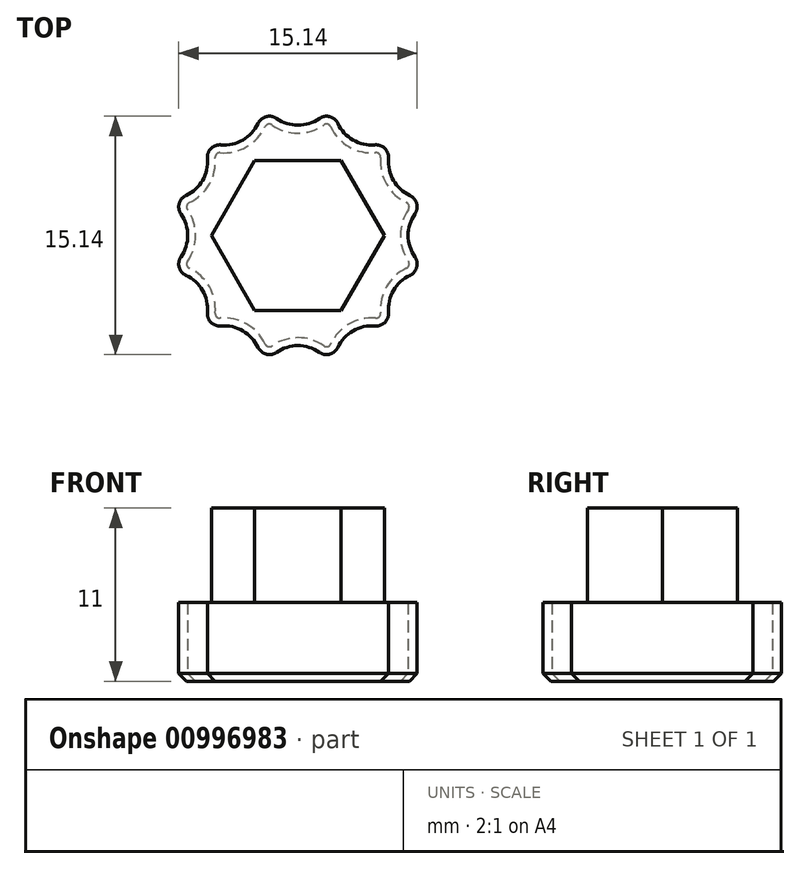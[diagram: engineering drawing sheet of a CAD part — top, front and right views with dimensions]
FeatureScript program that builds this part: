
annotation { "Feature Type Name" : "Feature", "Feature Type Description" : "" }
export const myFeature = defineFeature(function(context is Context, id is Id, definition is map)
    precondition{}
    {
        {
            var Q0;
            Q0=qCreatedBy(makeId("Top.planeOp"),FACE);
            var sketch = newSketch(context, id + "F0", { "sketchPlane" : qUnion([Q0])});
            skCircle(sketch, "E0", {"center": v(0, 0) * mm, "radius": 7 * mm, "construction": true});
            skArc(sketch, "E1", {"start": v(-1.36, 7.43) * mm, "mid": v(0, 7) * mm, "end": v(1.36, 7.43) * mm});
            skArc(sketch, "E2.1.0", {"start": v(-4.9, 5.75) * mm, "mid": v(-3.5, 6.06) * mm, "end": v(-2.53, 7.11) * mm});
            skArc(sketch, "E2.2.0", {"start": v(-7.11, 2.53) * mm, "mid": v(-6.06, 3.5) * mm, "end": v(-5.75, 4.9) * mm});
            skArc(sketch, "E2.3.0", {"start": v(-7.43, -1.36) * mm, "mid": v(-7, 0) * mm, "end": v(-7.43, 1.36) * mm});
            skArc(sketch, "E2.4.0", {"start": v(-5.75, -4.9) * mm, "mid": v(-6.06, -3.5) * mm, "end": v(-7.11, -2.53) * mm});
            skArc(sketch, "E2.5.0", {"start": v(-2.53, -7.11) * mm, "mid": v(-3.5, -6.06) * mm, "end": v(-4.9, -5.75) * mm});
            skArc(sketch, "E2.6.0", {"start": v(1.36, -7.43) * mm, "mid": v(0, -7) * mm, "end": v(-1.36, -7.43) * mm});
            skArc(sketch, "E2.7.0", {"start": v(4.9, -5.75) * mm, "mid": v(3.5, -6.06) * mm, "end": v(2.53, -7.11) * mm});
            skArc(sketch, "E2.8.0", {"start": v(7.11, -2.53) * mm, "mid": v(6.06, -3.5) * mm, "end": v(5.75, -4.9) * mm});
            skArc(sketch, "E2.9.0", {"start": v(7.43, 1.36) * mm, "mid": v(7, 0) * mm, "end": v(7.43, -1.36) * mm});
            skArc(sketch, "E2.10.0", {"start": v(5.75, 4.9) * mm, "mid": v(6.06, 3.5) * mm, "end": v(7.11, 2.53) * mm});
            skArc(sketch, "E2.11.0", {"start": v(2.53, 7.11) * mm, "mid": v(3.5, 6.06) * mm, "end": v(4.9, 5.75) * mm});
            skPoint(sketch, "E3.newPointA", {"position": v(1.9, 7.96) * mm});
            skPoint(sketch, "E3.newPointB", {"position": v(2.33, 7.85) * mm});
            skArc(sketch, "E3.filletArc", {"start": v(2.53, 7.11) * mm, "mid": v(2.02, 7.54) * mm, "end": v(1.36, 7.43) * mm});
            skPoint(sketch, "E4.newPointA", {"position": v(5.63, 5.94) * mm});
            skPoint(sketch, "E4.newPointB", {"position": v(5.94, 5.63) * mm});
            skArc(sketch, "E4.filletArc", {"start": v(5.75, 4.9) * mm, "mid": v(5.52, 5.52) * mm, "end": v(4.9, 5.75) * mm});
            skPoint(sketch, "E5.newPointA", {"position": v(7.85, 2.33) * mm});
            skPoint(sketch, "E5.newPointB", {"position": v(7.96, 1.9) * mm});
            skArc(sketch, "E5.filletArc", {"start": v(7.43, 1.36) * mm, "mid": v(7.54, 2.02) * mm, "end": v(7.11, 2.53) * mm});
            skPoint(sketch, "E6.newPointA", {"position": v(7.96, -1.9) * mm});
            skPoint(sketch, "E6.newPointB", {"position": v(7.85, -2.33) * mm});
            skArc(sketch, "E6.filletArc", {"start": v(7.11, -2.53) * mm, "mid": v(7.54, -2.02) * mm, "end": v(7.43, -1.36) * mm});
            skPoint(sketch, "E7.newPointA", {"position": v(5.94, -5.63) * mm});
            skPoint(sketch, "E7.newPointB", {"position": v(5.63, -5.94) * mm});
            skArc(sketch, "E7.filletArc", {"start": v(4.9, -5.75) * mm, "mid": v(5.52, -5.52) * mm, "end": v(5.75, -4.9) * mm});
            skPoint(sketch, "E8.newPointA", {"position": v(2.33, -7.85) * mm});
            skPoint(sketch, "E8.newPointB", {"position": v(1.9, -7.96) * mm});
            skArc(sketch, "E8.filletArc", {"start": v(1.36, -7.43) * mm, "mid": v(2.02, -7.54) * mm, "end": v(2.53, -7.11) * mm});
            skPoint(sketch, "E9.newPointA", {"position": v(-1.9, -7.96) * mm});
            skPoint(sketch, "E9.newPointB", {"position": v(-2.33, -7.85) * mm});
            skArc(sketch, "E9.filletArc", {"start": v(-2.53, -7.11) * mm, "mid": v(-2.02, -7.54) * mm, "end": v(-1.36, -7.43) * mm});
            skPoint(sketch, "E10.newPointA", {"position": v(-5.63, -5.94) * mm});
            skPoint(sketch, "E10.newPointB", {"position": v(-5.94, -5.63) * mm});
            skArc(sketch, "E10.filletArc", {"start": v(-5.75, -4.9) * mm, "mid": v(-5.52, -5.52) * mm, "end": v(-4.9, -5.75) * mm});
            skPoint(sketch, "E11.newPointA", {"position": v(-7.85, -2.33) * mm});
            skPoint(sketch, "E11.newPointB", {"position": v(-7.96, -1.9) * mm});
            skArc(sketch, "E11.filletArc", {"start": v(-7.43, -1.36) * mm, "mid": v(-7.54, -2.02) * mm, "end": v(-7.11, -2.53) * mm});
            skPoint(sketch, "E12.newPointA", {"position": v(-7.96, 1.9) * mm});
            skPoint(sketch, "E12.newPointB", {"position": v(-7.85, 2.33) * mm});
            skArc(sketch, "E12.filletArc", {"start": v(-7.11, 2.53) * mm, "mid": v(-7.54, 2.02) * mm, "end": v(-7.43, 1.36) * mm});
            skPoint(sketch, "E13.newPointA", {"position": v(-5.94, 5.63) * mm});
            skPoint(sketch, "E13.newPointB", {"position": v(-5.63, 5.94) * mm});
            skArc(sketch, "E13.filletArc", {"start": v(-4.9, 5.75) * mm, "mid": v(-5.52, 5.52) * mm, "end": v(-5.75, 4.9) * mm});
            skPoint(sketch, "E14.newPointA", {"position": v(-2.33, 7.85) * mm});
            skPoint(sketch, "E14.newPointB", {"position": v(-1.9, 7.96) * mm});
            skArc(sketch, "E14.filletArc", {"start": v(-1.36, 7.43) * mm, "mid": v(-2.02, 7.54) * mm, "end": v(-2.53, 7.11) * mm});
            skSolve(sketch);
        }
        {
            var Q0;
            Q0=makeQuery(id+"F0.imprint","IMPRINT",FACE,{"disambiguationData":[TD([[makeQuery(id+"F0.imprint","IMPRINT",EDGE,{"derivedFrom":sQuery(id+"F0.wireOp",EDGE,"E1")}),-1.0]])]});
            extrude(context, id + "F1", {"entities" : qUnion([Q0]), "depth" : 5 * mm, "offsetDistance" : 25 * mm});
        }
        {
            var Q0;
            Q0=makeQuery(id+"F1.opExtrude","CAP_FACE",FACE,{"disambiguationData":[OSD([sQuery(id+"F0.wireOp",EDGE,"E1"),sQuery(id+"F0.wireOp",EDGE,"E2.1.0"),sQuery(id+"F0.wireOp",EDGE,"E2.2.0"),sQuery(id+"F0.wireOp",EDGE,"E2.3.0"),sQuery(id+"F0.wireOp",EDGE,"E2.4.0"),sQuery(id+"F0.wireOp",EDGE,"E2.5.0"),sQuery(id+"F0.wireOp",EDGE,"E2.6.0"),sQuery(id+"F0.wireOp",EDGE,"E2.7.0"),sQuery(id+"F0.wireOp",EDGE,"E2.8.0"),sQuery(id+"F0.wireOp",EDGE,"E2.9.0"),sQuery(id+"F0.wireOp",EDGE,"E2.10.0"),sQuery(id+"F0.wireOp",EDGE,"E2.11.0"),sQuery(id+"F0.wireOp",EDGE,"E3.filletArc"),sQuery(id+"F0.wireOp",EDGE,"E4.filletArc"),sQuery(id+"F0.wireOp",EDGE,"E5.filletArc"),sQuery(id+"F0.wireOp",EDGE,"E6.filletArc"),sQuery(id+"F0.wireOp",EDGE,"E7.filletArc"),sQuery(id+"F0.wireOp",EDGE,"E8.filletArc"),sQuery(id+"F0.wireOp",EDGE,"E9.filletArc"),sQuery(id+"F0.wireOp",EDGE,"E10.filletArc"),sQuery(id+"F0.wireOp",EDGE,"E11.filletArc"),sQuery(id+"F0.wireOp",EDGE,"E12.filletArc"),sQuery(id+"F0.wireOp",EDGE,"E13.filletArc"),sQuery(id+"F0.wireOp",EDGE,"E14.filletArc")])],"isStart":false});
            var sketch = newSketch(context, id + "F2", { "sketchPlane" : qUnion([Q0])});
            skCircle(sketch, "E15.cCircle", {"center": v(0, 0) * mm, "radius": 5.5 * mm, "construction": true});
            skLineSegment(sketch, "E15.0", {"start": v(2.75, -4.76) * mm, "end": v(-2.75, -4.76) * mm});
            skLineSegment(sketch, "E15.1", {"start": v(-2.75, -4.76) * mm, "end": v(-5.5, 0) * mm});
            skLineSegment(sketch, "E15.2", {"start": v(-5.5, 0) * mm, "end": v(-2.75, 4.76) * mm});
            skLineSegment(sketch, "E15.3", {"start": v(-2.75, 4.76) * mm, "end": v(2.75, 4.76) * mm});
            skLineSegment(sketch, "E15.4", {"start": v(2.75, 4.76) * mm, "end": v(5.5, 0) * mm});
            skLineSegment(sketch, "E15.5", {"start": v(5.5, 0) * mm, "end": v(2.75, -4.76) * mm});
            skSolve(sketch);
        }
        {
            var Q0;
            Q0 = qSketchRegion(id + "F2", true);
            extrude(context, id + "F3", {"entities" : qUnion([Q0]), "operationType" : NewBodyOperationType.ADD, "depth" : 6 * mm, "offsetDistance" : 25 * mm});
        }
        {
            var Q0;
            Q0=makeQuery(id+"F1.opExtrude","CAP_FACE",FACE,{"disambiguationData":[OSD([sQuery(id+"F0.wireOp",EDGE,"E1"),sQuery(id+"F0.wireOp",EDGE,"E2.1.0"),sQuery(id+"F0.wireOp",EDGE,"E2.2.0"),sQuery(id+"F0.wireOp",EDGE,"E2.3.0"),sQuery(id+"F0.wireOp",EDGE,"E2.4.0"),sQuery(id+"F0.wireOp",EDGE,"E2.5.0"),sQuery(id+"F0.wireOp",EDGE,"E2.6.0"),sQuery(id+"F0.wireOp",EDGE,"E2.7.0"),sQuery(id+"F0.wireOp",EDGE,"E2.8.0"),sQuery(id+"F0.wireOp",EDGE,"E2.9.0"),sQuery(id+"F0.wireOp",EDGE,"E2.10.0"),sQuery(id+"F0.wireOp",EDGE,"E2.11.0"),sQuery(id+"F0.wireOp",EDGE,"E3.filletArc"),sQuery(id+"F0.wireOp",EDGE,"E4.filletArc"),sQuery(id+"F0.wireOp",EDGE,"E5.filletArc"),sQuery(id+"F0.wireOp",EDGE,"E6.filletArc"),sQuery(id+"F0.wireOp",EDGE,"E7.filletArc"),sQuery(id+"F0.wireOp",EDGE,"E8.filletArc"),sQuery(id+"F0.wireOp",EDGE,"E9.filletArc"),sQuery(id+"F0.wireOp",EDGE,"E10.filletArc"),sQuery(id+"F0.wireOp",EDGE,"E11.filletArc"),sQuery(id+"F0.wireOp",EDGE,"E12.filletArc"),sQuery(id+"F0.wireOp",EDGE,"E13.filletArc"),sQuery(id+"F0.wireOp",EDGE,"E14.filletArc")])],"isStart":true});
            chamfer(context, id + "F4", {"entities" : qUnion([Q0]), "width" : .5 * mm, "tangentPropagation" : true});
        }
    });
